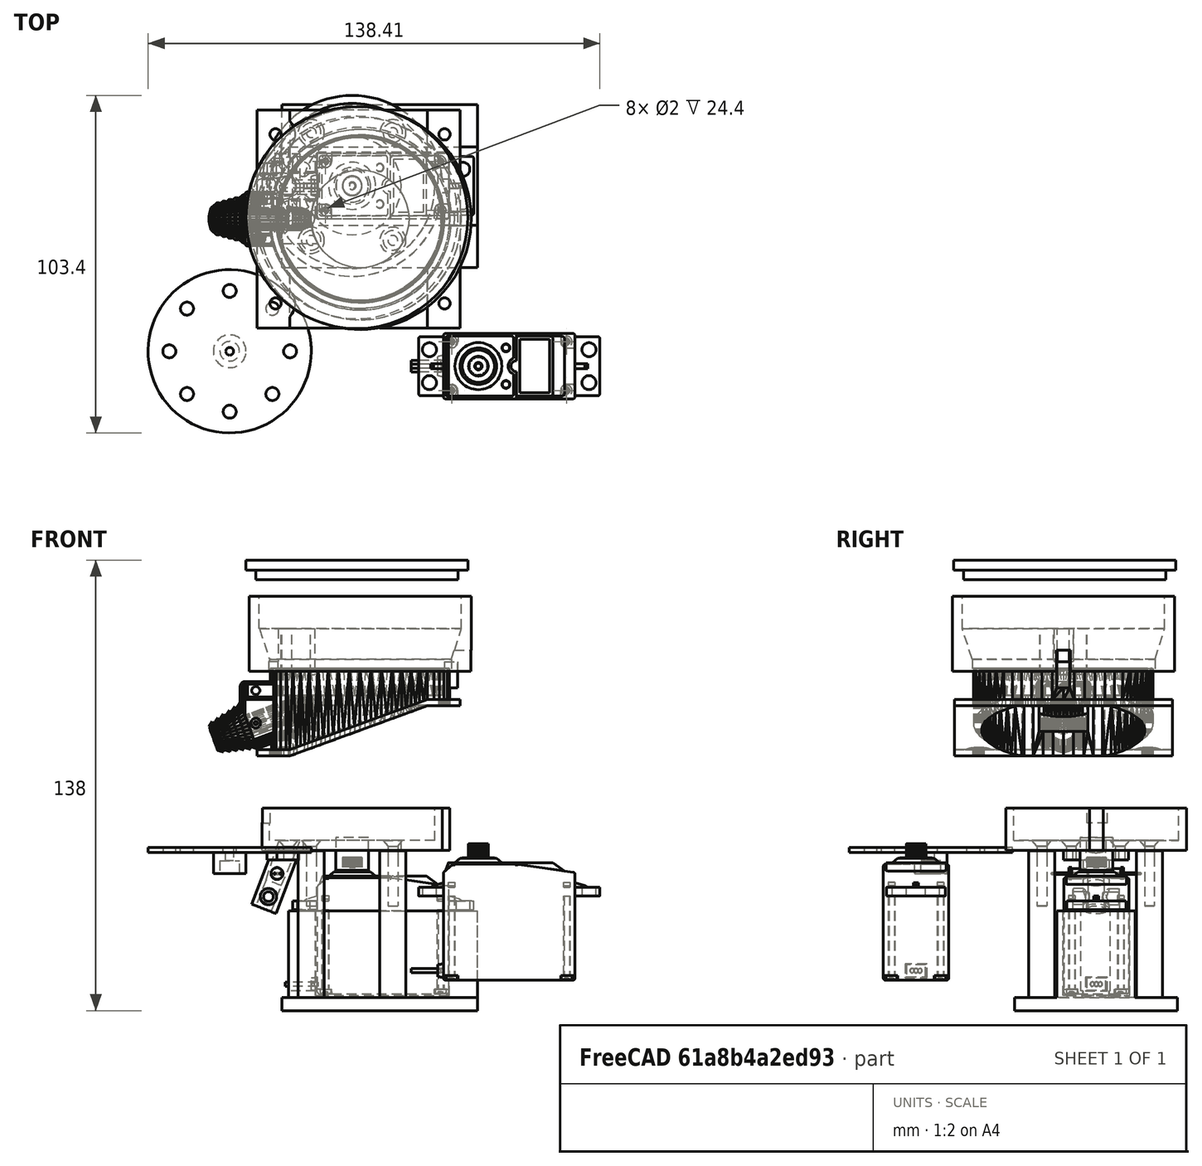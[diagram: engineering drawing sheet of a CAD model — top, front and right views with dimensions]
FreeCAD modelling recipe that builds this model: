
FCSTD DOCUMENT  (FreeCAD 0.21R33694 (Git))
Label: all_parts_chute_with_mount_v5
License: All rights reserved
LicenseURL: http://en.wikipedia.org/wiki/All_rights_reserved
objects: Part::Cylinder×34, Part::Cut×23, Part::MultiFuse×21, Part::Feature×18, Part::Box×11, Part::FeaturePython×5, Part::Cone×2, Sketcher::SketchObject×2, Part::Extrusion×2, Mesh::Feature×1, Part::Fillet×1, Part::Chamfer×1
note: 120 computed .brp shape members not serialized (recipe doc carries the construction recipe); baked Part::Feature solids carry a one-line shape summary decoded from their .brp

FEATURE [Part::Box] Box014  label="Cube014"
  AttacherType = Attacher::AttachEngine3D
  Height = 13
  Length = 4.2
  Placement = pos=(66.2,37.3,63.6) rot=(0,0,1;0rad)
  Width = 4.2
FEATURE [Part::Cylinder] Cylinder022
  Angle = 360
  AttacherType = Attacher::AttachEngine3D
  FirstAngle = 0
  Height = 20
  Placement = pos=(15.5,39.3,51.5) rot=(0,1,0;0.366519rad)
  Radius = 3
  SecondAngle = 0
FEATURE [Part::Box] Box015  label="Cube015"
  AttacherType = Attacher::AttachEngine3D
  Height = 10
  Length = 10
  Placement = pos=(7,36.6,72) rot=(0,0,1;0rad)
  Width = 6.2
FEATURE [Mesh::Feature] Base_V7  label="Base V7"
FEATURE [Part::Feature] Base_V7001_solid  label="hopper (Solid)"
  shape: bbox 76.98 x 66.8 x 28.84 mm, 5900 faces (baked)
FEATURE [Part::Feature] Shape001
  Placement = pos=(47,50.7,-44.8) rot=(0,0,1;3.14159rad)
  shape: bbox 57.75 x 20 x 41.74 mm, 378 faces, 4 solids (baked)
FEATURE [Part::Cylinder] cylinder010  label="servo_central_shaft"
  Angle = 360
  AttacherType = Attacher::AttachEngine3D
  FirstAngle = 0
  Height = 10
  Placement = pos=(37.55,50.7,-7) rot=(0,0,1;0rad)
  Radius = 5
  SecondAngle = 0
FEATURE [Part::Box] Box  label="Cube"
  AttacherType = Attacher::AttachEngine3D
  Height = 27.5
  Length = 58
  Placement = pos=(18,38.6,-47) rot=(0,0,1;0rad)
  Width = 24
FEATURE [Part::Box] Box016  label="Cube016"
  AttacherType = Attacher::AttachEngine3D
  Height = 29.5
  Length = 53
  Placement = pos=(13,46,-44) rot=(0,0,1;0rad)
  Width = 9
FEATURE [Part::Cut] Cut
  Base = -> Box
  Tool = -> Box016
FEATURE [Part::Box] Box017  label="Cube017"
  AttacherType = Attacher::AttachEngine3D
  Height = 29.5
  Length = 10
  Placement = pos=(17,46.6,-46) rot=(0,0,1;0rad)
  Width = 8
FEATURE [Part::Cut] Cut019
  Base = -> Cut
  Tool = -> Box017
FEATURE [Part::Box] Box018  label="Cube018"
  AttacherType = Attacher::AttachEngine3D
  Height = 27.5
  Length = 41
  Placement = pos=(0.5,50.4,-44.2) rot=(0,0,1;0rad)
  Width = 20.4
FEATURE [Part::Fillet] Fillet
  Base = -> Box018
  Edges = 4 edges r=1: [Edge1,Edge3,Edge5,Edge7]
  Placement = pos=(25.85,-9.87885,-1.16822) rot=(0,0,1;0rad)
FEATURE [Part::Cut] Cut020
  Base = -> Cut019
  Tool = -> Fillet
FEATURE [Part::Box] Box020  label="base_plate"
  AttacherType = Attacher::AttachEngine3D
  Height = 4
  Length = 60
  Placement = pos=(16,25.6,-50) rot=(0,0,1;0rad)
  Width = 50
FEATURE [Part::Feature] BOLTS_part  label="Hex socket countersunk head screw M3 20.0"
  Placement = pos=(25,67,2.1) rot=(0,1,0;3.14159rad)
  shape: bbox 6 x 6 x 20 mm, 12 faces (baked)
FEATURE [Part::Feature] BOLTS_part001  label="Hex socket countersunk head screw M3 20.001"
  Placement = pos=(50,67,2.1) rot=(0,1,0;3.14159rad)
  shape: bbox 6 x 6 x 20 mm, 12 faces (baked)
FEATURE [Part::Feature] BOLTS_part002  label="Hex socket countersunk head screw M3 20.002"
  Placement = pos=(50,34,2.1) rot=(0,1,0;3.14159rad)
  shape: bbox 6 x 6 x 20 mm, 12 faces (baked)
FEATURE [Part::Feature] BOLTS_part003  label="Hex socket countersunk head screw M3 20.003"
  Placement = pos=(25,34,2.1) rot=(0,1,0;3.14159rad)
  shape: bbox 6 x 6 x 20 mm, 12 faces (baked)
FEATURE [Part::Cylinder] Cylinder024
  Angle = 360
  AttacherType = Attacher::AttachEngine3D
  FirstAngle = 0
  Height = 48
  Placement = pos=(50,67,-49) rot=(0,0,1;0rad)
  Radius = 4
  SecondAngle = 0
FEATURE [Part::Cylinder] Cylinder025
  Angle = 360
  AttacherType = Attacher::AttachEngine3D
  FirstAngle = 0
  Height = 48
  Placement = pos=(25,34,-49) rot=(0,0,1;0rad)
  Radius = 4
  SecondAngle = 0
FEATURE [Part::Cylinder] Cylinder026
  Angle = 360
  AttacherType = Attacher::AttachEngine3D
  FirstAngle = 0
  Height = 48
  Placement = pos=(25,67,-49) rot=(0,0,1;0rad)
  Radius = 4
  SecondAngle = 0
FEATURE [Part::Cylinder] Cylinder027
  Angle = 360
  AttacherType = Attacher::AttachEngine3D
  FirstAngle = 0
  Height = 48
  Placement = pos=(50,34,-49) rot=(0,0,1;0rad)
  Radius = 4
  SecondAngle = 0
FEATURE [Part::Feature] Shape002  label="led2"
  Placement = pos=(14.5,42.3,-8) rot=(-1,0,0;1.5708rad)
  shape: bbox 3.686 x 11.4 x 3.686 mm, 26 faces, 3 solids (baked)
FEATURE [Part::Feature] Shape003  label="led1"
  Placement = pos=(14.5,59.1,-8) rot=(1,0,0;1.5708rad)
  shape: bbox 3.686 x 11.4 x 3.686 mm, 26 faces, 3 solids (baked)
FEATURE [Part::Feature] BOLTS_part004  label="Hex socket countersunk head screw M3 20.004"
  Placement = pos=(25,34,2.05) rot=(0,1,0;3.14159rad)
  shape: bbox 6 x 6 x 20 mm, 12 faces (baked)
FEATURE [Part::Feature] BOLTS_part005  label="Hex socket countersunk head screw M3 20.005"
  Placement = pos=(50,34,2.05) rot=(0,1,0;3.14159rad)
  shape: bbox 6 x 6 x 20 mm, 12 faces (baked)
FEATURE [Part::Feature] BOLTS_part006  label="Hex socket countersunk head screw M3 20.006"
  Placement = pos=(50,67,2.05) rot=(0,1,0;3.14159rad)
  shape: bbox 6 x 6 x 20 mm, 12 faces (baked)
FEATURE [Part::Feature] BOLTS_part007  label="Hex socket countersunk head screw M3 20.007"
  Placement = pos=(25,67,2.05) rot=(0,1,0;3.14159rad)
  shape: bbox 6 x 6 x 20 mm, 12 faces (baked)
FEATURE [Part::Cylinder] Cylinder032
  Angle = 360
  AttacherType = Attacher::AttachEngine3D
  FirstAngle = 0
  Height = 48
  Placement = pos=(50,67,-43) rot=(0,0,1;0rad)
  Radius = 1.4
  SecondAngle = 0
FEATURE [Part::Cylinder] Cylinder033
  Angle = 360
  AttacherType = Attacher::AttachEngine3D
  FirstAngle = 0
  Height = 48
  Placement = pos=(25,34,-43) rot=(0,0,1;0rad)
  Radius = 1.4
  SecondAngle = 0
FEATURE [Part::Cylinder] Cylinder034
  Angle = 360
  AttacherType = Attacher::AttachEngine3D
  FirstAngle = 0
  Height = 48
  Placement = pos=(25,67,-42) rot=(0,0,1;0rad)
  Radius = 1.4
  SecondAngle = 0
FEATURE [Part::Cylinder] Cylinder035
  Angle = 360
  AttacherType = Attacher::AttachEngine3D
  FirstAngle = 0
  Height = 48
  Placement = pos=(50,34,-43) rot=(0,0,1;0rad)
  Radius = 1.4
  SecondAngle = 0
FEATURE [Part::Cut] Cut030
  Base = -> Cylinder024
  Tool = -> BOLTS_part006
FEATURE [Part::Cut] Cut031
  Base = -> Cylinder025
  Tool = -> BOLTS_part004
FEATURE [Part::Cut] Cut032
  Base = -> Cylinder026
  Tool = -> BOLTS_part007
FEATURE [Part::Cut] Cut033
  Base = -> Cylinder027
  Tool = -> BOLTS_part005
FEATURE [Part::MultiFuse] Fusion011  label="motor_holder"
  Shapes = -> [Cut020,Cut030,Cut031,Cut032,Cut033,Box020]
FEATURE [Part::Cylinder] Cylinder039
  Angle = 360
  AttacherType = Attacher::AttachEngine3D
  FirstAngle = 0
  Height = 21
  Placement = pos=(0,10,4) rot=(1,0,0;1.5708rad)
  Radius = 1.5
  SecondAngle = 0
FEATURE [Part::FeaturePython] Tube003  # WARN: FeaturePython — macro-defined, semantics opaque (R4)
  AttacherType = Attacher::AttachEngine3D
  Height = 5
  InnerRadius = 1.5
  OuterRadius = 2.5
  Placement = pos=(0,2.05,4) rot=(-1,0,0;1.5708rad)
FEATURE [Part::FeaturePython] Tube004  # WARN: FeaturePython — macro-defined, semantics opaque (R4)
  AttacherType = Attacher::AttachEngine3D
  Height = 5
  InnerRadius = 1.5
  OuterRadius = 2.5
  Placement = pos=(0,-2.05,4) rot=(1,0,0;1.5708rad)
FEATURE [Part::Box] Box021  label="Cube019"
  AttacherType = Attacher::AttachEngine3D
  Height = 10
  Length = 20
  Placement = pos=(1.17,-11.94,17.9) rot=(0,0,1;0rad)
  Width = 24
FEATURE [Part::FeaturePython] Tube001  # WARN: FeaturePython — macro-defined, semantics opaque (R4)
  AttacherType = Attacher::AttachEngine3D
  Height = 3
  InnerRadius = 15
  OuterRadius = 27.7
  Placement = pos=(40.45,39.4,63.6) rot=(0,0,1;0rad)
FEATURE [Part::FeaturePython] Tube002  # WARN: FeaturePython — macro-defined, semantics opaque (R4)
  AttacherType = Attacher::AttachEngine3D
  Height = 13
  InnerRadius = 25.3
  OuterRadius = 27.7
  Placement = pos=(40.45,39.4,63.6) rot=(0,0,1;0rad)
FEATURE [Part::MultiFuse] Fusion009
  Shapes = -> [Box014,Tube001,Tube002]
FEATURE [Part::Cut] Cut014  label="cut"
  Base = -> Fusion009
  Tool = -> Cylinder022
FEATURE [Part::Cut] Cut036
  Base = -> Cut014
  Placement = pos=(-2.9,11.3,-64.5) rot=(0,0,1;0rad)
  Tool = -> Box015
FEATURE [Part::MultiFuse] Fusion
  Shapes = -> [BOLTS_part003,Cylinder033]
FEATURE [Part::MultiFuse] Fusion013
  Shapes = -> [BOLTS_part002,Cylinder035]
FEATURE [Part::MultiFuse] Fusion014
  Shapes = -> [BOLTS_part001,Cylinder032]
FEATURE [Part::MultiFuse] Fusion015
  Shapes = -> [BOLTS_part,Cylinder034]
FEATURE [Part::Cut] Cut037
  Base = -> Cut036
  Tool = -> Fusion
FEATURE [Part::Cut] Cut038
  Base = -> Cut037
  Tool = -> Fusion013
FEATURE [Part::Cut] Cut039
  Base = -> Cut038
  Tool = -> Fusion015
FEATURE [Part::Cut] Cut040
  Base = -> Cut039
  Tool = -> Fusion014
FEATURE [Part::Feature] BOLTS_part009  label="Hex socket countersunk head screw M3 20.008"
  Placement = pos=(50,34,2.1) rot=(0,1,0;3.14159rad)
  shape: bbox 6 x 6 x 20 mm, 12 faces (baked)
FEATURE [Part::Cylinder] Cylinder040
  Angle = 360
  AttacherType = Attacher::AttachEngine3D
  FirstAngle = 0
  Height = 48
  Placement = pos=(50,34,-43) rot=(0,0,1;0rad)
  Radius = 1.4
  SecondAngle = 0
FEATURE [Part::MultiFuse] Fusion016
  Placement = pos=(-32,9,0) rot=(0,0,1;0rad)
  Shapes = -> [BOLTS_part009,Cylinder040]
FEATURE [Part::Feature] BOLTS_part010  label="Hex socket countersunk head screw M3 20.009"
  Placement = pos=(50,34,2.1) rot=(0,1,0;3.14159rad)
  shape: bbox 6 x 6 x 20 mm, 12 faces (baked)
FEATURE [Part::Cylinder] Cylinder041
  Angle = 360
  AttacherType = Attacher::AttachEngine3D
  FirstAngle = 0
  Height = 48
  Placement = pos=(50,34,-43) rot=(0,0,1;0rad)
  Radius = 1.4
  SecondAngle = 0
FEATURE [Part::MultiFuse] Fusion017
  Placement = pos=(-32,24,0) rot=(0,0,1;0rad)
  Shapes = -> [BOLTS_part010,Cylinder041]
FEATURE [Part::Box] Box022  label="Cube020"
  AttacherType = Attacher::AttachEngine3D
  Height = 3
  Length = 10
  Placement = pos=(3,-10,15) rot=(0,0,1;0rad)
  Width = 20
FEATURE [Part::Cylinder] Cylinder
  Angle = 360
  AttacherType = Attacher::AttachEngine3D
  FirstAngle = 0
  Height = 18
  Radius = 4
  SecondAngle = 0
FEATURE [Part::Cut] Cut043
  Base = -> Cylinder
  Tool = -> Cylinder039
FEATURE [Part::MultiFuse] Fusion018
  Placement = pos=(2,0,0) rot=(0,1,0;0.366519rad)
  Shapes = -> [Tube003,Tube004,Cut043]
FEATURE [Part::MultiFuse] Fusion019
  Shapes = -> [Fusion018,Box022]
FEATURE [Part::Feature] BOLTS_part011  label="Hex socket countersunk head screw M3 20.010"
  Placement = pos=(50,34,2.1) rot=(0,1,0;3.14159rad)
  shape: bbox 6 x 6 x 20 mm, 12 faces (baked)
FEATURE [Part::Cylinder] Cylinder044
  Angle = 360
  AttacherType = Attacher::AttachEngine3D
  FirstAngle = 0
  Height = 48
  Placement = pos=(50,34,-43) rot=(0,0,1;0rad)
  Radius = 1.4
  SecondAngle = 0
FEATURE [Part::MultiFuse] Fusion021
  Placement = pos=(-32,9,0) rot=(0,0,1;0rad)
  Shapes = -> [BOLTS_part011,Cylinder044]
FEATURE [Part::Feature] BOLTS_part012  label="Hex socket countersunk head screw M3 20.011"
  Placement = pos=(50,34,2.1) rot=(0,1,0;3.14159rad)
  shape: bbox 6 x 6 x 20 mm, 12 faces (baked)
FEATURE [Part::Cylinder] Cylinder045
  Angle = 360
  AttacherType = Attacher::AttachEngine3D
  FirstAngle = 0
  Height = 48
  Placement = pos=(50,34,-43) rot=(0,0,1;0rad)
  Radius = 1.4
  SecondAngle = 0
FEATURE [Part::MultiFuse] Fusion022
  Placement = pos=(-32,24,0) rot=(0,0,1;0rad)
  Shapes = -> [BOLTS_part012,Cylinder045]
FEATURE [Part::Cut] Cut047
  Base = -> Cut040
  Tool = -> Fusion016
FEATURE [Part::Cut] Cut048  label="base"
  Base = -> Cut047
  Tool = -> Fusion017
FEATURE [Part::Feature] Shape004
  Placement = pos=(85.6641,-4.55315,-40.6487) rot=(0,0,1;3.14159rad)
  shape: bbox 57.75 x 20 x 41.74 mm, 378 faces, 4 solids (baked)
FEATURE [Part::Box] Box012  label="Cube012"
  AttacherType = Attacher::AttachEngine3D
  Height = 10
  Length = 10
  Placement = pos=(7,36.17,76) rot=(0,0,1;0rad)
  Width = 6
FEATURE [Part::Box] Box013  label="Cube013"
  AttacherType = Attacher::AttachEngine3D
  Height = 10
  Length = 14
  Placement = pos=(64,38.5,50.5) rot=(0,0,1;0rad)
  Width = 4.3
FEATURE [Part::Cone] Cone
  Angle = 360
  AttacherType = Attacher::AttachEngine3D
  Height = 14
  Placement = pos=(40,40.65,53) rot=(0,0,1;0rad)
  Radius1 = 26.5
  Radius2 = 31
FEATURE [Part::Cylinder] Cylinder019
  Angle = 360
  AttacherType = Attacher::AttachEngine3D
  FirstAngle = 0
  Height = 13
  Placement = pos=(40,40.65,54) rot=(0,0,1;0rad)
  Radius = 34
  SecondAngle = 0
FEATURE [Part::Cylinder] Cylinder020
  Angle = 360
  AttacherType = Attacher::AttachEngine3D
  FirstAngle = 0
  Height = 13
  Placement = pos=(40,39.2,54) rot=(0,0,1;0rad)
  Radius = 25
  SecondAngle = 0
FEATURE [Part::Cylinder] Cylinder021
  Angle = 360
  AttacherType = Attacher::AttachEngine3D
  FirstAngle = 0
  Height = 4
  Placement = pos=(40,40.65,54) rot=(0,0,1;0rad)
  Radius = 28
  SecondAngle = 0
FEATURE [Sketcher::SketchObject] Sketch001
  FullyConstrained = true
  MapMode = 2
  Placement = pos=(0,5,65) rot=(0,0,1;0rad)
  sketch-geometry (8):
    g0: ArcOfCircle CenterX=20.555 CenterY=41.4363 CenterZ=0 NormalX=0 NormalY=0 NormalZ=1 AngleXU=0 Radius=4.5 StartAngle=3.17145 EndAngle=4.38602
    g1: ArcOfCircle CenterX=24.0176 CenterY=34.022 CenterZ=0 NormalX=0 NormalY=0 NormalZ=1 AngleXU=0 Radius=2 StartAngle=5.10518 EndAngle=7.46119
    g2: ArcOfCircle CenterX=20.5312 CenterY=26.882 CenterZ=0 NormalX=0 NormalY=0 NormalZ=1 AngleXU=0 Radius=4.5 StartAngle=1.8916 EndAngle=3.11914
    g3: LineSegment StartX=19.1123 StartY=31.1525 StartZ=0 EndX=24.7831 EndY=32.1743 EndZ=0
    g4: LineSegment StartX=19.1123 StartY=37.1738 StartZ=0 EndX=24.7831 EndY=35.8697 EndZ=0
    g5: LineSegment StartX=16.057 StartY=41.302 StartZ=0 EndX=15.8089 EndY=41.3763 EndZ=0
    g6: LineSegment StartX=15.8133 StartY=26.9187 StartZ=0 EndX=16.0324 EndY=26.9831 EndZ=0
    g7: ArcOfCircle CenterX=39.7432 CenterY=34.1548 CenterZ=0 NormalX=0 NormalY=0 NormalZ=1 AngleXU=0 Radius=25 StartAngle=2.84856 EndAngle=3.43524
  constraints (28):
    c: Coincident(g3,g2)
    c: Coincident(g3,g1)
    c: Coincident(g4,g0)
    c: Coincident(g4,g1)
    c: Coincident(g5,g0)
    c: Coincident(g6,g2)
    c: Coincident(g7,g6)
    c: Coincident(g7,g5)
    c: Radius(g2) = 4.5
    c: Radius(g0) = 4.5
    c: Radius(g1) = 2
    c: Radius(g7) = 25
    c: DistanceX(g5) = 15.8089
    c: DistanceY(g5) = 41.3763
    c: DistanceX(g2) = 16.0324
    c: DistanceY(g2) = 26.9831
    c: DistanceX(g3) = 19.1123
    c: DistanceY(g3) = 31.1525
    c: DistanceX(g2,g0) = 0
    c: DistanceX(g3,g1) = 0
    c: DistanceX(g1) = 24.7831
    c: DistanceY(g1) = 32.1743
    c: DistanceX(g5) = 16.057
    c: DistanceY(g5) = 41.302
    c: DistanceX(g7) = 15.8133
    c: DistanceY(g7) = 26.9187
    c: DistanceY(g1) = 35.8697
    c: DistanceY(g0) = 37.1738
FEATURE [Part::Extrusion] Extrude001
  Base = -> Sketch001
  Dir = (0,0,1)
  DirMode = 2
  FaceMakerClass = Part::FaceMakerBullseye
  LengthFwd = 14
  LengthRev = 0
  Placement = pos=(0,0,7) rot=(0,0,1;0rad)
  Solid = true
  Symmetric = false
FEATURE [Part::MultiFuse] Fusion006  label="pellet_sorter"
  Placement = pos=(0,1.5,-19) rot=(0,0,1;0rad)
  Shapes = -> [Box012,Extrude001]
FEATURE [Part::FeaturePython] Tube  # WARN: FeaturePython — macro-defined, semantics opaque (R4)
  AttacherType = Attacher::AttachEngine3D
  Height = 23
  InnerRadius = 31
  OuterRadius = 34
  Placement = pos=(40,40.65,54) rot=(0,0,1;0rad)
FEATURE [Part::MultiFuse] Fusion010
  Shapes = -> [Tube,Cylinder019,Cylinder020]
FEATURE [Part::Cut] Cut015
  Base = -> Fusion010
  Tool = -> Cone
FEATURE [Part::Cut] Cut016
  Base = -> Cut015
  Tool = -> Cylinder021
FEATURE [Part::MultiFuse] Fusion024
  Shapes = -> [Fusion006,Cut016]
FEATURE [Part::Cut] Cut017  label="lid"
  Base = -> Fusion024
  Tool = -> Box013
FEATURE [Part::Cylinder] Cylinder047
  Angle = 360
  AttacherType = Attacher::AttachEngine3D
  FirstAngle = 0
  Height = 3
  Radius = 34
  SecondAngle = 0
FEATURE [Part::Cylinder] Cylinder048
  Angle = 360
  AttacherType = Attacher::AttachEngine3D
  FirstAngle = 0
  Height = 6
  Radius = 31
  SecondAngle = 0
FEATURE [Part::MultiFuse] Fusion025  label="cap"
  Placement = pos=(39,41,88) rot=(1,0,0;3.14159rad)
  Shapes = -> [Cylinder047,Cylinder048]
FEATURE [Part::Cylinder] cylinder012
  Angle = 360
  AttacherType = Attacher::AttachEngine3D
  FirstAngle = 0
  Height = 1.5
  Radius = 25
  SecondAngle = 0
FEATURE [Part::Cylinder] cylinder013
  Angle = 360
  AttacherType = Attacher::AttachEngine3D
  FirstAngle = 0
  Height = 5
  Placement = pos=(18.5,0,0) rot=(0,0,1;0rad)
  Radius = 2
  SecondAngle = 0
FEATURE [Part::Cylinder] cylinder014
  Angle = 360
  AttacherType = Attacher::AttachEngine3D
  FirstAngle = 0
  Height = 5
  Placement = pos=(13.0815,13.0815,0) rot=(0,0,1;0.785398rad)
  Radius = 2
  SecondAngle = 0
FEATURE [Part::Cylinder] cylinder015
  Angle = 360
  AttacherType = Attacher::AttachEngine3D
  FirstAngle = 0
  Height = 5
  Placement = pos=(0,18.5,0) rot=(0,0,1;1.5708rad)
  Radius = 2
  SecondAngle = 0
FEATURE [Part::Cylinder] cylinder016
  Angle = 360
  AttacherType = Attacher::AttachEngine3D
  FirstAngle = 0
  Height = 5
  Placement = pos=(-13.0815,13.0815,0) rot=(0,0,1;2.35619rad)
  Radius = 2
  SecondAngle = 0
FEATURE [Part::Cylinder] cylinder017
  Angle = 360
  AttacherType = Attacher::AttachEngine3D
  FirstAngle = 0
  Height = 5
  Placement = pos=(-18.5,2e-15,0) rot=(0,0,1;3.14159rad)
  Radius = 2
  SecondAngle = 0
FEATURE [Part::Cylinder] cylinder018
  Angle = 360
  AttacherType = Attacher::AttachEngine3D
  FirstAngle = 0
  Height = 5
  Placement = pos=(-13.0815,-13.0815,0) rot=(0,0,1;3.92699rad)
  Radius = 2
  SecondAngle = 0
FEATURE [Part::Cylinder] cylinder019
  Angle = 360
  AttacherType = Attacher::AttachEngine3D
  FirstAngle = 0
  Height = 5
  Placement = pos=(0,-18.5,0) rot=(0,0,-1;1.5708rad)
  Radius = 2
  SecondAngle = 0
FEATURE [Part::Cylinder] cylinder020
  Angle = 360
  AttacherType = Attacher::AttachEngine3D
  FirstAngle = 0
  Height = 5
  Placement = pos=(13.0815,-13.0815,0) rot=(0,0,-1;0.785398rad)
  Radius = 2
  SecondAngle = 0
FEATURE [Part::MultiFuse] Group001
  Placement = pos=(0,0,-1) rot=(0,0,1;0rad)
  Shapes = -> [cylinder013,cylinder014,cylinder015,cylinder016,cylinder017,cylinder018,cylinder019,cylinder020]
FEATURE [Part::Feature] Shape005
  Placement = pos=(85.6641,-4.55315,-40.6487) rot=(0,0,1;3.14159rad)
  shape: bbox 57.75 x 20 x 41.74 mm, 378 faces, 4 solids (baked)
FEATURE [Part::Cylinder] cylinder021  label="servo_central_shaft002"
  Angle = 360
  AttacherType = Attacher::AttachEngine3D
  FirstAngle = 0
  Height = 8
  Radius = 5
  SecondAngle = 0
FEATURE [Sketcher::SketchObject] Sketch002
  FullyConstrained = false
  MapMode = 5
  Placement = pos=(85.6641,-4.55315,1.09128) rot=(0,0,1;3.14159rad)
  Support = -> [Shape005]
  sketch-geometry (1):
    g0: Circle CenterX=9.4502 CenterY=-0.000218 CenterZ=0 NormalX=0 NormalY=0 NormalZ=1 AngleXU=0 Radius=3
  constraints (1):
    c: Radius(g0) = 3
FEATURE [Part::Extrusion] Extrude002
  Base = -> Sketch002
  Dir = (0,0,1)
  DirMode = 2
  FaceMakerClass = Part::FaceMakerBullseye
  LengthFwd = 6
  LengthRev = 0
  Placement = pos=(-76.21,4.55,3) rot=(0,0,1;0rad)
  Solid = true
  Symmetric = false
FEATURE [Part::Cylinder] Cylinder049
  Angle = 360
  AttacherType = Attacher::AttachEngine3D
  FirstAngle = 0
  Height = 19
  Placement = pos=(0,0,-1) rot=(0,0,1;0rad)
  Radius = 1.2
  SecondAngle = 0
FEATURE [Part::MultiFuse] Fusion026
  Shapes = -> [Group001,Extrude002,Cylinder049]
FEATURE [Part::MultiFuse] Fusion027
  Shapes = -> [cylinder012,cylinder021]
FEATURE [Part::Cut] Cut050  label="rotor001"
  Base = -> Fusion027
  Placement = pos=(0,0,0) rot=(1,0,0;3.14159rad)
  Tool = -> Fusion026
FEATURE [Part::Cone] Cone001
  Angle = 360
  AttacherType = Attacher::AttachEngine3D
  Height = 11
  Placement = pos=(0,-29,0) rot=(0,0,1;0rad)
  Radius1 = 2.5
  Radius2 = 3
FEATURE [Part::Cylinder] Cylinder050
  Angle = 360
  AttacherType = Attacher::AttachEngine3D
  FirstAngle = 0
  Height = 10
  Placement = pos=(0,-29,-10) rot=(0,0,1;0rad)
  Radius = 2.5
  SecondAngle = 0
FEATURE [Part::Cylinder] Cylinder051
  Angle = 360
  AttacherType = Attacher::AttachEngine3D
  FirstAngle = 0
  Height = 14
  Placement = pos=(0,-29,11) rot=(0,0,1;0rad)
  Radius = 3
  SecondAngle = 0
FEATURE [Part::MultiFuse] Fusion028
  Placement = pos=(5,29,8) rot=(0,1,0;0.366519rad)
  Shapes = -> [Cone001,Cylinder050,Cylinder051]
FEATURE [Part::MultiFuse] Fusion020
  Shapes = -> [Box021,Fusion028]
FEATURE [Part::Cut] Cut044  label="foodchute"
  Base = -> Fusion019
  Placement = pos=(8.45427,50.6,-18.8) rot=(0,0,1;0rad)
  Tool = -> Fusion020
FEATURE [Part::Chamfer] Chamfer
  Base = -> Cut044
  Edges = 2 edges r=3: [Edge1,Edge3]
FEATURE [Part::Cut] Cut045
  Base = -> Chamfer
  Tool = -> Fusion021
FEATURE [Part::Cut] Cut046  label="chute_with_mount"
  Base = -> Cut045
  Tool = -> Fusion022
